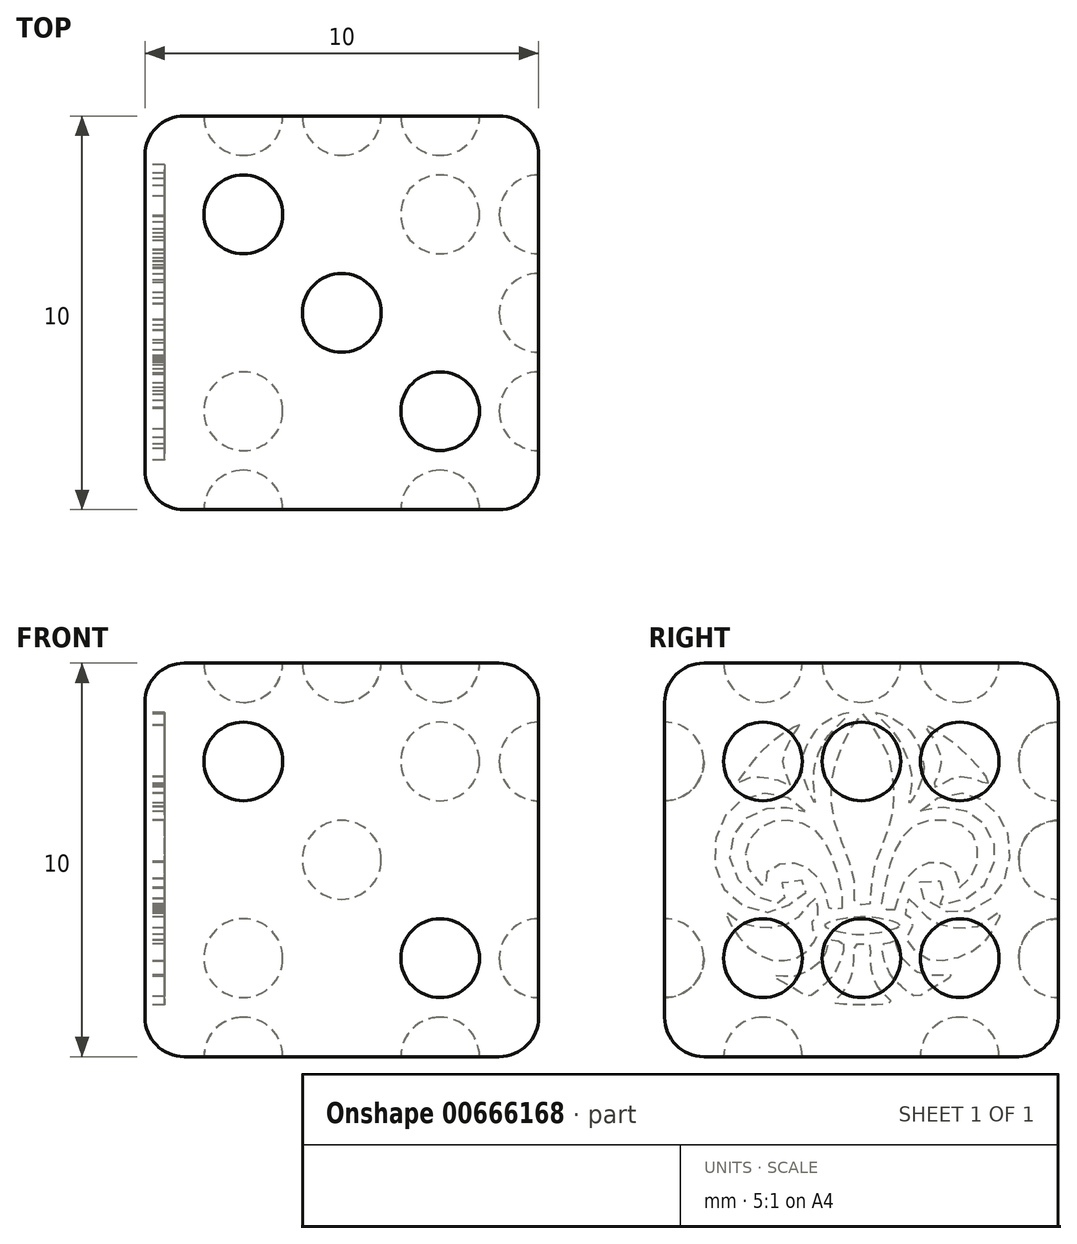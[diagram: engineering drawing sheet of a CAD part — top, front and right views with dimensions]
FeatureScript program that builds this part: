
annotation { "Feature Type Name" : "Feature", "Feature Type Description" : "" }
export const myFeature = defineFeature(function(context is Context, id is Id, definition is map)
    precondition{}
    {
        {
            var Q0;
            Q0=qCreatedBy(makeId("Front.planeOp"),FACE);
            var sketch = newSketch(context, id + "F0", { "sketchPlane" : qUnion([Q0])});
            skLineSegment(sketch, "E0.bottom", {"start": v(-26.81, 13.83) * mm, "end": v(-36.81, 13.83) * mm});
            skLineSegment(sketch, "E0.top", {"start": v(-26.81, 3.83) * mm, "end": v(-36.81, 3.83) * mm});
            skLineSegment(sketch, "E0.left", {"start": v(-26.81, 13.83) * mm, "end": v(-26.81, 3.83) * mm});
            skLineSegment(sketch, "E0.right", {"start": v(-36.81, 13.83) * mm, "end": v(-36.81, 3.83) * mm});
            skPoint(sketch, "E0.middle", {"position": v(-31.81, 8.83) * mm});
            skSolve(sketch);
        }
        {
            var Q0;
            Q0=makeQuery(id+"F0.imprint","IMPRINT",FACE,{"disambiguationData":[TD([[makeQuery(id+"F0.imprint","IMPRINT",EDGE,{"derivedFrom":sQuery(id+"F0.wireOp",EDGE,"E0.bottom")}),1.0]])]});
            extrude(context, id + "F1", {"entities" : qUnion([Q0]), "depth" : 10 * mm, "offsetDistance" : 25 * mm});
        }
        {
            var Q0;
            Q0=makeQuery(id+"F1.opExtrude","CAP_EDGE",EDGE,{"disambiguationData":[OSD([sQuery(id+"F0.wireOp",EDGE,"E0.bottom")])],"isStart":false});
            var Q1;
            Q1=makeQuery(id+"F1.opExtrude","CAP_EDGE",EDGE,{"disambiguationData":[OSD([sQuery(id+"F0.wireOp",EDGE,"E0.left")])],"isStart":false});
            var Q2;
            Q2=makeQuery(id+"F1.opExtrude","CAP_EDGE",EDGE,{"disambiguationData":[OSD([sQuery(id+"F0.wireOp",EDGE,"E0.right")])],"isStart":false});
            var Q3;
            Q3=makeQuery(id+"F1.opExtrude","CAP_EDGE",EDGE,{"disambiguationData":[OSD([sQuery(id+"F0.wireOp",EDGE,"E0.top")])],"isStart":false});
            var Q4;
            Q4=makeQuery(id+"F1.opExtrude","SWEPT_EDGE",EDGE,{"disambiguationData":[OSD([sQuery(id+"F0.wireOp",EDGE,"E0.bottom"),sQuery(id+"F0.wireOp",EDGE,"E0.left")])]});
            var Q5;
            Q5=makeQuery(id+"F1.opExtrude","SWEPT_EDGE",EDGE,{"disambiguationData":[OSD([sQuery(id+"F0.wireOp",EDGE,"E0.top"),sQuery(id+"F0.wireOp",EDGE,"E0.left")])]});
            var Q6;
            Q6=makeQuery(id+"F1.opExtrude","CAP_EDGE",EDGE,{"disambiguationData":[OSD([sQuery(id+"F0.wireOp",EDGE,"E0.left")])],"isStart":true});
            var Q7;
            Q7=makeQuery(id+"F1.opExtrude","SWEPT_EDGE",EDGE,{"disambiguationData":[OSD([sQuery(id+"F0.wireOp",EDGE,"E0.bottom"),sQuery(id+"F0.wireOp",EDGE,"E0.right")])]});
            var Q8;
            Q8=makeQuery(id+"F1.opExtrude","CAP_EDGE",EDGE,{"disambiguationData":[OSD([sQuery(id+"F0.wireOp",EDGE,"E0.right")])],"isStart":true});
            var Q9;
            Q9=makeQuery(id+"F1.opExtrude","SWEPT_EDGE",EDGE,{"disambiguationData":[OSD([sQuery(id+"F0.wireOp",EDGE,"E0.top"),sQuery(id+"F0.wireOp",EDGE,"E0.right")])]});
            var Q10;
            Q10=makeQuery(id+"F1.opExtrude","CAP_EDGE",EDGE,{"disambiguationData":[OSD([sQuery(id+"F0.wireOp",EDGE,"E0.top")])],"isStart":true});
            var Q11;
            Q11=makeQuery(id+"F1.opExtrude","CAP_EDGE",EDGE,{"disambiguationData":[OSD([sQuery(id+"F0.wireOp",EDGE,"E0.bottom")])],"isStart":true});
            fillet(context, id + "F2", {"entities" : qUnion([Q0, Q1, Q2, Q3, Q4, Q5, Q6, Q7, Q8, Q9, Q10, Q11]), "radius" : 1 * mm, "tangentPropagation" : true, "allowEdgeOverflow" : false});
        }
        {
            var Q0;
            Q0=makeQuery(id+"F1.opExtrude","CAP_FACE",FACE,{"disambiguationData":[OSD([sQuery(id+"F0.wireOp",EDGE,"E0.bottom"),sQuery(id+"F0.wireOp",EDGE,"E0.top"),sQuery(id+"F0.wireOp",EDGE,"E0.left"),sQuery(id+"F0.wireOp",EDGE,"E0.right")])],"isStart":false});
            var sketch = newSketch(context, id + "F3", { "sketchPlane" : qUnion([Q0])});
            skCircle(sketch, "E1", {"center": v(-34.31, 11.33) * mm, "radius": 1 * mm});
            skCircle(sketch, "E2", {"center": v(-29.31, 6.33) * mm, "radius": 1 * mm});
            skSolve(sketch);
        }
        {
            var Q0;
            Q0=makeQuery(id+"F3.imprint","IMPRINT",FACE,{"disambiguationData":[TD([[makeQuery(id+"F3.imprint","IMPRINT",EDGE,{"derivedFrom":sQuery(id+"F3.wireOp",EDGE,"E1")}),1.0]])]});
            var Q1;
            Q1=makeQuery(id+"F3.imprint","IMPRINT",FACE,{"disambiguationData":[TD([[makeQuery(id+"F3.imprint","IMPRINT",EDGE,{"derivedFrom":sQuery(id+"F3.wireOp",EDGE,"E2")}),1.0]])]});
            extrude(context, id + "F4", {"entities" : qUnion([Q0, Q1]), "operationType" : NewBodyOperationType.REMOVE, "oppositeDirection" : true, "depth" : 1 * mm, "offsetDistance" : 25 * mm});
        }
        {
            var Q0;
            Q0=makeQuery(id+"F4.boolean.opBoolean","COPY",EDGE,{"derivedFrom":makeQuery(id+"F4.opExtrude","CAP_EDGE",EDGE,{"disambiguationData":[OSD([sQuery(id+"F3.wireOp",EDGE,"E1")])],"isStart":false})});
            var Q1;
            Q1=makeQuery(id+"F4.boolean.opBoolean","COPY",EDGE,{"derivedFrom":makeQuery(id+"F4.opExtrude","CAP_EDGE",EDGE,{"disambiguationData":[OSD([sQuery(id+"F3.wireOp",EDGE,"E2")])],"isStart":false})});
            fillet(context, id + "F5", {"entities" : qUnion([Q0, Q1]), "radius" : 1 * mm, "tangentPropagation" : true, "allowEdgeOverflow" : false});
        }
        {
            var Q0;
            Q0=makeQuery(id+"F1.opExtrude","CAP_FACE",FACE,{"disambiguationData":[OSD([sQuery(id+"F0.wireOp",EDGE,"E0.bottom"),sQuery(id+"F0.wireOp",EDGE,"E0.top"),sQuery(id+"F0.wireOp",EDGE,"E0.left"),sQuery(id+"F0.wireOp",EDGE,"E0.right")])],"isStart":true});
            var sketch = newSketch(context, id + "F6", { "sketchPlane" : qUnion([Q0])});
            skCircle(sketch, "E3", {"center": v(29.31, 11.33) * mm, "radius": 1 * mm});
            skCircle(sketch, "E4", {"center": v(34.31, 11.33) * mm, "radius": 1 * mm});
            skCircle(sketch, "E5", {"center": v(34.31, 6.33) * mm, "radius": 1 * mm});
            skCircle(sketch, "E6", {"center": v(29.31, 6.33) * mm, "radius": 1 * mm});
            skCircle(sketch, "E7", {"center": v(31.81, 8.83) * mm, "radius": 1 * mm});
            skSolve(sketch);
        }
        {
            var Q0;
            Q0=makeQuery(id+"F6.imprint","IMPRINT",FACE,{"disambiguationData":[TD([[makeQuery(id+"F6.imprint","IMPRINT",EDGE,{"derivedFrom":sQuery(id+"F6.wireOp",EDGE,"E3")}),1.0]])]});
            var Q1;
            Q1=makeQuery(id+"F6.imprint","IMPRINT",FACE,{"disambiguationData":[TD([[makeQuery(id+"F6.imprint","IMPRINT",EDGE,{"derivedFrom":sQuery(id+"F6.wireOp",EDGE,"E4")}),1.0]])]});
            var Q2;
            Q2=makeQuery(id+"F6.imprint","IMPRINT",FACE,{"disambiguationData":[TD([[makeQuery(id+"F6.imprint","IMPRINT",EDGE,{"derivedFrom":sQuery(id+"F6.wireOp",EDGE,"E7")}),1.0]])]});
            var Q3;
            Q3=makeQuery(id+"F6.imprint","IMPRINT",FACE,{"disambiguationData":[TD([[makeQuery(id+"F6.imprint","IMPRINT",EDGE,{"derivedFrom":sQuery(id+"F6.wireOp",EDGE,"E5")}),1.0]])]});
            var Q4;
            Q4=makeQuery(id+"F6.imprint","IMPRINT",FACE,{"disambiguationData":[TD([[makeQuery(id+"F6.imprint","IMPRINT",EDGE,{"derivedFrom":sQuery(id+"F6.wireOp",EDGE,"E6")}),1.0]])]});
            extrude(context, id + "F7", {"entities" : qUnion([Q0, Q1, Q2, Q3, Q4]), "operationType" : NewBodyOperationType.REMOVE, "oppositeDirection" : true, "depth" : 1 * mm, "offsetDistance" : 25 * mm});
        }
        {
            var Q0;
            Q0=makeQuery(id+"F7.boolean.opBoolean","COPY",EDGE,{"derivedFrom":makeQuery(id+"F7.opExtrude","CAP_EDGE",EDGE,{"disambiguationData":[OSD([sQuery(id+"F6.wireOp",EDGE,"E6")])],"isStart":false})});
            var Q1;
            Q1=makeQuery(id+"F7.boolean.opBoolean","COPY",EDGE,{"derivedFrom":makeQuery(id+"F7.opExtrude","CAP_EDGE",EDGE,{"disambiguationData":[OSD([sQuery(id+"F6.wireOp",EDGE,"E3")])],"isStart":false})});
            var Q2;
            Q2=makeQuery(id+"F7.boolean.opBoolean","COPY",EDGE,{"derivedFrom":makeQuery(id+"F7.opExtrude","CAP_EDGE",EDGE,{"disambiguationData":[OSD([sQuery(id+"F6.wireOp",EDGE,"E7")])],"isStart":false})});
            var Q3;
            Q3=makeQuery(id+"F7.boolean.opBoolean","COPY",EDGE,{"derivedFrom":makeQuery(id+"F7.opExtrude","CAP_EDGE",EDGE,{"disambiguationData":[OSD([sQuery(id+"F6.wireOp",EDGE,"E4")])],"isStart":false})});
            var Q4;
            Q4=makeQuery(id+"F7.boolean.opBoolean","COPY",EDGE,{"derivedFrom":makeQuery(id+"F7.opExtrude","CAP_EDGE",EDGE,{"disambiguationData":[OSD([sQuery(id+"F6.wireOp",EDGE,"E5")])],"isStart":false})});
            fillet(context, id + "F8", {"entities" : qUnion([Q0, Q1, Q2, Q3, Q4]), "radius" : 1 * mm, "tangentPropagation" : true, "allowEdgeOverflow" : false});
        }
        {
            var Q0;
            Q0=makeQuery(id+"F1.opExtrude","SWEPT_FACE",FACE,{"disambiguationData":[OSD([sQuery(id+"F0.wireOp",EDGE,"E0.bottom")])]});
            var sketch = newSketch(context, id + "F9", { "sketchPlane" : qUnion([Q0])});
            skCircle(sketch, "E8", {"center": v(-34.31, -2.5) * mm, "radius": 1 * mm});
            skCircle(sketch, "E9", {"center": v(-31.81, -5) * mm, "radius": 1 * mm});
            skCircle(sketch, "E10", {"center": v(-29.31, -7.5) * mm, "radius": 1 * mm});
            skSolve(sketch);
        }
        {
            var Q0;
            Q0=makeQuery(id+"F9.imprint","IMPRINT",FACE,{"disambiguationData":[TD([[makeQuery(id+"F9.imprint","IMPRINT",EDGE,{"derivedFrom":sQuery(id+"F9.wireOp",EDGE,"E8")}),1.0]])]});
            var Q1;
            Q1=makeQuery(id+"F9.imprint","IMPRINT",FACE,{"disambiguationData":[TD([[makeQuery(id+"F9.imprint","IMPRINT",EDGE,{"derivedFrom":sQuery(id+"F9.wireOp",EDGE,"E9")}),1.0]])]});
            var Q2;
            Q2=makeQuery(id+"F9.imprint","IMPRINT",FACE,{"disambiguationData":[TD([[makeQuery(id+"F9.imprint","IMPRINT",EDGE,{"derivedFrom":sQuery(id+"F9.wireOp",EDGE,"E10")}),1.0]])]});
            extrude(context, id + "F10", {"entities" : qUnion([Q0, Q1, Q2]), "operationType" : NewBodyOperationType.REMOVE, "oppositeDirection" : true, "depth" : 1 * mm, "offsetDistance" : 25 * mm});
        }
        {
            var Q0;
            Q0=makeQuery(id+"F10.boolean.opBoolean","COPY",EDGE,{"derivedFrom":makeQuery(id+"F10.opExtrude","CAP_EDGE",EDGE,{"disambiguationData":[OSD([sQuery(id+"F9.wireOp",EDGE,"E8")])],"isStart":false})});
            var Q1;
            Q1=makeQuery(id+"F10.boolean.opBoolean","COPY",EDGE,{"derivedFrom":makeQuery(id+"F10.opExtrude","CAP_EDGE",EDGE,{"disambiguationData":[OSD([sQuery(id+"F9.wireOp",EDGE,"E9")])],"isStart":false})});
            var Q2;
            Q2=makeQuery(id+"F10.boolean.opBoolean","COPY",EDGE,{"derivedFrom":makeQuery(id+"F10.opExtrude","CAP_EDGE",EDGE,{"disambiguationData":[OSD([sQuery(id+"F9.wireOp",EDGE,"E10")])],"isStart":false})});
            fillet(context, id + "F11", {"entities" : qUnion([Q0, Q1, Q2]), "radius" : 1 * mm, "tangentPropagation" : true, "allowEdgeOverflow" : false});
        }
        {
            var Q0;
            Q0=makeQuery(id+"F1.opExtrude","SWEPT_FACE",FACE,{"disambiguationData":[OSD([sQuery(id+"F0.wireOp",EDGE,"E0.top")])]});
            var sketch = newSketch(context, id + "F12", { "sketchPlane" : qUnion([Q0])});
            skCircle(sketch, "E11", {"center": v(-34.31, 7.5) * mm, "radius": 1 * mm});
            skCircle(sketch, "E12", {"center": v(-29.31, 7.5) * mm, "radius": 1 * mm});
            skCircle(sketch, "E13", {"center": v(-34.31, 2.5) * mm, "radius": 1 * mm});
            skCircle(sketch, "E14", {"center": v(-29.31, 2.5) * mm, "radius": 1 * mm});
            skSolve(sketch);
        }
        {
            var Q0;
            Q0=makeQuery(id+"F12.imprint","IMPRINT",FACE,{"disambiguationData":[TD([[makeQuery(id+"F12.imprint","IMPRINT",EDGE,{"derivedFrom":sQuery(id+"F12.wireOp",EDGE,"E11")}),1.0]])]});
            var Q1;
            Q1=makeQuery(id+"F12.imprint","IMPRINT",FACE,{"disambiguationData":[TD([[makeQuery(id+"F12.imprint","IMPRINT",EDGE,{"derivedFrom":sQuery(id+"F12.wireOp",EDGE,"E12")}),1.0]])]});
            var Q2;
            Q2=makeQuery(id+"F12.imprint","IMPRINT",FACE,{"disambiguationData":[TD([[makeQuery(id+"F12.imprint","IMPRINT",EDGE,{"derivedFrom":sQuery(id+"F12.wireOp",EDGE,"E13")}),1.0]])]});
            var Q3;
            Q3=makeQuery(id+"F12.imprint","IMPRINT",FACE,{"disambiguationData":[TD([[makeQuery(id+"F12.imprint","IMPRINT",EDGE,{"derivedFrom":sQuery(id+"F12.wireOp",EDGE,"E14")}),1.0]])]});
            extrude(context, id + "F13", {"entities" : qUnion([Q0, Q1, Q2, Q3]), "operationType" : NewBodyOperationType.REMOVE, "oppositeDirection" : true, "depth" : 1 * mm, "offsetDistance" : 25 * mm});
        }
        {
            var Q0;
            Q0=makeQuery(id+"F13.boolean.opBoolean","COPY",EDGE,{"derivedFrom":makeQuery(id+"F13.opExtrude","CAP_EDGE",EDGE,{"disambiguationData":[OSD([sQuery(id+"F12.wireOp",EDGE,"E11")])],"isStart":false})});
            var Q1;
            Q1=makeQuery(id+"F13.boolean.opBoolean","COPY",FACE,{"derivedFrom":makeQuery(id+"F13.opExtrude","CAP_FACE",FACE,{"disambiguationData":[OSD([sQuery(id+"F12.wireOp",EDGE,"E12")])],"isStart":false})});
            var Q2;
            Q2=makeQuery(id+"F13.boolean.opBoolean","COPY",FACE,{"derivedFrom":makeQuery(id+"F13.opExtrude","CAP_FACE",FACE,{"disambiguationData":[OSD([sQuery(id+"F12.wireOp",EDGE,"E13")])],"isStart":false})});
            var Q3;
            Q3=makeQuery(id+"F13.boolean.opBoolean","COPY",FACE,{"derivedFrom":makeQuery(id+"F13.opExtrude","CAP_FACE",FACE,{"disambiguationData":[OSD([sQuery(id+"F12.wireOp",EDGE,"E14")])],"isStart":false})});
            fillet(context, id + "F14", {"entities" : qUnion([Q0, Q1, Q2, Q3]), "radius" : 1 * mm, "tangentPropagation" : true, "allowEdgeOverflow" : false});
        }
        {
            var Q0;
            Q0=makeQuery(id+"F1.opExtrude","SWEPT_FACE",FACE,{"disambiguationData":[OSD([sQuery(id+"F0.wireOp",EDGE,"E0.left")])]});
            var sketch = newSketch(context, id + "F15", { "sketchPlane" : qUnion([Q0])});
            skPoint(sketch, "E15.center.orphan", {"position": v(-2.5, 6.33) * mm});
            skPoint(sketch, "E16.center.orphan", {"position": v(-5, 6.33) * mm});
            skPoint(sketch, "E17.center.orphan", {"position": v(-7.5, 6.33) * mm});
            skPoint(sketch, "E18.center.orphan", {"position": v(-7.5, 11.33) * mm});
            skPoint(sketch, "E19.center.orphan", {"position": v(-5, 11.33) * mm});
            skPoint(sketch, "E20.center.orphan", {"position": v(-2.5, 11.33) * mm});
            skCircle(sketch, "E21", {"center": v(-2.5, 6.33) * mm, "radius": 1 * mm});
            skCircle(sketch, "E22", {"center": v(-5, 6.33) * mm, "radius": 1 * mm});
            skCircle(sketch, "E23", {"center": v(-7.5, 6.33) * mm, "radius": 1 * mm});
            skCircle(sketch, "E24", {"center": v(-2.5, 11.33) * mm, "radius": 1 * mm});
            skCircle(sketch, "E25", {"center": v(-5, 11.33) * mm, "radius": 1 * mm});
            skCircle(sketch, "E26", {"center": v(-7.5, 11.33) * mm, "radius": 1 * mm});
            skSolve(sketch);
        }
        {
            var Q0;
            Q0=makeQuery(id+"F15.imprint","IMPRINT",FACE,{"disambiguationData":[TD([[makeQuery(id+"F15.imprint","IMPRINT",EDGE,{"derivedFrom":sQuery(id+"F15.wireOp",EDGE,"E18")}),1.0]])]});
            var Q1;
            Q1=makeQuery(id+"F15.imprint","IMPRINT",FACE,{"disambiguationData":[TD([[makeQuery(id+"F15.imprint","IMPRINT",EDGE,{"derivedFrom":sQuery(id+"F15.wireOp",EDGE,"E17")}),1.0]])]});
            var Q2;
            Q2=makeQuery(id+"F15.imprint","IMPRINT",FACE,{"disambiguationData":[TD([[makeQuery(id+"F15.imprint","IMPRINT",EDGE,{"derivedFrom":sQuery(id+"F15.wireOp",EDGE,"E21")}),1.0]])]});
            var Q3;
            Q3=makeQuery(id+"F15.imprint","IMPRINT",FACE,{"disambiguationData":[TD([[makeQuery(id+"F15.imprint","IMPRINT",EDGE,{"derivedFrom":sQuery(id+"F15.wireOp",EDGE,"E22")}),1.0]])]});
            var Q4;
            Q4=makeQuery(id+"F15.imprint","IMPRINT",FACE,{"disambiguationData":[TD([[makeQuery(id+"F15.imprint","IMPRINT",EDGE,{"derivedFrom":sQuery(id+"F15.wireOp",EDGE,"E23")}),1.0]])]});
            var Q5;
            Q5=makeQuery(id+"F15.imprint","IMPRINT",FACE,{"disambiguationData":[TD([[makeQuery(id+"F15.imprint","IMPRINT",EDGE,{"derivedFrom":sQuery(id+"F15.wireOp",EDGE,"E26")}),1.0]])]});
            var Q6;
            Q6=makeQuery(id+"F15.imprint","IMPRINT",FACE,{"disambiguationData":[TD([[makeQuery(id+"F15.imprint","IMPRINT",EDGE,{"derivedFrom":sQuery(id+"F15.wireOp",EDGE,"E25")}),1.0]])]});
            var Q7;
            Q7=makeQuery(id+"F15.imprint","IMPRINT",FACE,{"disambiguationData":[TD([[makeQuery(id+"F15.imprint","IMPRINT",EDGE,{"derivedFrom":sQuery(id+"F15.wireOp",EDGE,"E24")}),1.0]])]});
            extrude(context, id + "F16", {"entities" : qUnion([Q0, Q1, Q2, Q3, Q4, Q5, Q6, Q7]), "operationType" : NewBodyOperationType.REMOVE, "oppositeDirection" : true, "depth" : 1 * mm, "offsetDistance" : 25 * mm});
        }
        {
            var Q0;
            Q0=makeQuery(id+"F16.boolean.opBoolean","COPY",EDGE,{"derivedFrom":makeQuery(id+"F16.opExtrude","CAP_EDGE",EDGE,{"disambiguationData":[OSD([sQuery(id+"F15.wireOp",EDGE,"E21")])],"isStart":false})});
            var Q1;
            Q1=makeQuery(id+"F16.boolean.opBoolean","COPY",EDGE,{"derivedFrom":makeQuery(id+"F16.opExtrude","CAP_EDGE",EDGE,{"disambiguationData":[OSD([sQuery(id+"F15.wireOp",EDGE,"E22")])],"isStart":false})});
            var Q2;
            Q2=makeQuery(id+"F16.boolean.opBoolean","COPY",EDGE,{"derivedFrom":makeQuery(id+"F16.opExtrude","CAP_EDGE",EDGE,{"disambiguationData":[OSD([sQuery(id+"F15.wireOp",EDGE,"E23")])],"isStart":false})});
            var Q3;
            Q3=makeQuery(id+"F16.boolean.opBoolean","COPY",EDGE,{"derivedFrom":makeQuery(id+"F16.opExtrude","CAP_EDGE",EDGE,{"disambiguationData":[OSD([sQuery(id+"F15.wireOp",EDGE,"E24")])],"isStart":false})});
            var Q4;
            Q4=makeQuery(id+"F16.boolean.opBoolean","COPY",EDGE,{"derivedFrom":makeQuery(id+"F16.opExtrude","CAP_EDGE",EDGE,{"disambiguationData":[OSD([sQuery(id+"F15.wireOp",EDGE,"E25")])],"isStart":false})});
            var Q5;
            Q5=makeQuery(id+"F16.boolean.opBoolean","COPY",EDGE,{"derivedFrom":makeQuery(id+"F16.opExtrude","CAP_EDGE",EDGE,{"disambiguationData":[OSD([sQuery(id+"F15.wireOp",EDGE,"E26")])],"isStart":false})});
            fillet(context, id + "F17", {"entities" : qUnion([Q0, Q1, Q2, Q3, Q4, Q5]), "radius" : 1 * mm, "tangentPropagation" : true, "allowEdgeOverflow" : false});
        }
        {
            var Q0;
            Q0=makeQuery(id+"F1.opExtrude","SWEPT_FACE",FACE,{"disambiguationData":[OSD([sQuery(id+"F0.wireOp",EDGE,"E0.right")])]});
            var sketch = newSketch(context, id + "F18", { "sketchPlane" : qUnion([Q0])});
            skFitSpline(sketch, "E27", {"points": [v(1.77, 10.79) * mm, v(2.2, 11.39) * mm, v(2.6, 11.75) * mm, v(3.08, 12.09) * mm, v(3.4, 12.24) * mm, v(3.23, 12) * mm, v(3.04, 11.6) * mm, v(3, 11.16) * mm, v(3.16, 10.69) * mm, v(2.77, 10.86) * mm, v(2.26, 10.93) * mm, v(1.77, 10.79) * mm]});
            skFitSpline(sketch, "E28", {"points": [v(3.5, 10.07) * mm, v(3.06, 10.4) * mm, v(2.38, 10.52) * mm, v(2, 10.38) * mm, v(1.54, 10) * mm, v(1.28, 9.48) * mm, v(1.25, 8.74) * mm, v(1.44, 8.16) * mm, v(1.87, 7.71) * mm, v(2.52, 7.47) * mm, v(3.08, 7.63) * mm, v(3.61, 8.13) * mm, v(3.22, 8.36) * mm, v(2.9, 8.2) * mm, v(2.92, 7.93) * mm, v(3.07, 7.72) * mm, v(2.52, 7.78) * mm, v(1.93, 8.13) * mm, v(1.63, 8.73) * mm, v(1.6, 9.11) * mm, v(1.84, 9.7) * mm, v(2.27, 10.03) * mm, v(2.83, 10.18) * mm, v(3.5, 10.07) * mm]});
            skFitSpline(sketch, "E29", {"points": [v(4.15, 7.57) * mm, v(3.98, 8.12) * mm, v(3.62, 8.6) * mm, v(3.15, 8.78) * mm, v(2.7, 8.66) * mm, v(2.54, 8.4) * mm, v(2.54, 8.11) * mm, v(2.16, 8.48) * mm, v(2.04, 9) * mm, v(2.17, 9.48) * mm, v(2.65, 9.79) * mm, v(3.39, 9.8) * mm, v(3.86, 9.53) * mm, v(4.16, 9.03) * mm, v(4.35, 8.4) * mm, v(4.46, 7.6) * mm, v(4.3, 7.58) * mm, v(4.15, 7.57) * mm]});
            skFitSpline(sketch, "E30", {"points": [v(3.78, 7.84) * mm, v(3.45, 7.5) * mm, v(2.92, 7.16) * mm, v(2.28, 7.1) * mm, v(1.88, 7.23) * mm, v(1.46, 7.53) * mm, v(1.66, 7.07) * mm, v(2.08, 6.56) * mm, v(2.78, 6.29) * mm, v(3.43, 6.35) * mm, v(3.85, 6.88) * mm, v(3.74, 7.02) * mm, v(3.69, 7.18) * mm, v(3.77, 7.37) * mm, v(3.86, 7.42) * mm, v(3.85, 7.64) * mm, v(3.78, 7.84) * mm]});
            skFitSpline(sketch, "E31", {"points": [v(4.02, 7.16) * mm, v(4.23, 7.28) * mm, v(4.8, 7.37) * mm, v(5.33, 7.35) * mm, v(5.95, 7.17) * mm, v(5.4, 6.97) * mm, v(4.73, 6.96) * mm, v(4.02, 7.16) * mm]});
            skFitSpline(sketch, "E32", {"points": [v(4.63, 12.57) * mm, v(4.07, 12.35) * mm, v(3.68, 12) * mm, v(3.44, 11.42) * mm, v(3.49, 10.8) * mm, v(3.78, 10.27) * mm, v(3.71, 10.72) * mm, v(3.8, 11.31) * mm, v(3.99, 11.78) * mm, v(4.24, 12.15) * mm, v(4.63, 12.57) * mm]});
            skFitSpline(sketch, "E33", {"points": [v(4.97, 12.54) * mm, v(4.73, 12.21) * mm, v(4.39, 11.67) * mm, v(4.24, 11.15) * mm, v(4.17, 10.3) * mm, v(4.28, 9.73) * mm, v(4.55, 9) * mm, v(4.73, 8.43) * mm, v(4.8, 7.68) * mm, v(4.95, 7.69) * mm, v(5.13, 7.69) * mm, v(5.17, 8.21) * mm, v(5.36, 8.95) * mm, v(5.68, 9.83) * mm, v(5.77, 10.6) * mm, v(5.64, 11.3) * mm, v(5.36, 11.99) * mm, v(4.97, 12.54) * mm]});
            skFitSpline(sketch, "E34", {"points": [v(5.31, 12.57) * mm, v(5.95, 12.3) * mm, v(6.3, 11.9) * mm, v(6.53, 11.3) * mm, v(6.43, 10.8) * mm, v(6.18, 10.27) * mm, v(6.21, 10.79) * mm, v(6.12, 11.44) * mm, v(5.78, 12.06) * mm, v(5.31, 12.57) * mm]});
            skFitSpline(sketch, "E35", {"points": [v(6.57, 12.25) * mm, v(7.26, 11.84) * mm, v(7.87, 11.2) * mm, v(8.17, 10.77) * mm, v(7.97, 10.87) * mm, v(7.46, 10.93) * mm, v(6.96, 10.79) * mm, v(6.8, 10.7) * mm, v(6.96, 11.14) * mm, v(6.93, 11.61) * mm, v(6.7, 12.05) * mm, v(6.57, 12.25) * mm]});
            skFitSpline(sketch, "E36", {"points": [v(6.43, 10.06) * mm, v(6.83, 10.4) * mm, v(7.45, 10.52) * mm, v(8.05, 10.35) * mm, v(8.5, 9.9) * mm, v(8.72, 9.27) * mm, v(8.67, 8.45) * mm, v(8.26, 7.83) * mm, v(7.57, 7.5) * mm, v(6.98, 7.6) * mm, v(6.54, 7.91) * mm, v(6.33, 8.14) * mm, v(6.62, 8.34) * mm, v(7.04, 8.22) * mm, v(7.03, 7.97) * mm, v(6.9, 7.73) * mm, v(7.3, 7.76) * mm, v(7.75, 7.95) * mm, v(8.25, 8.52) * mm, v(8.32, 9.08) * mm, v(8.15, 9.64) * mm, v(7.77, 10) * mm, v(7.2, 10.18) * mm, v(6.78, 10.14) * mm, v(6.43, 10.06) * mm]});
            skFitSpline(sketch, "E37", {"points": [v(5.48, 7.6) * mm, v(5.55, 8.3) * mm, v(5.8, 9.05) * mm, v(6.16, 9.58) * mm, v(6.6, 9.78) * mm, v(7.12, 9.82) * mm, v(7.6, 9.62) * mm, v(7.9, 9.16) * mm, v(7.86, 8.58) * mm, v(7.42, 8.13) * mm, v(7.43, 8.41) * mm, v(7.12, 8.7) * mm, v(6.6, 8.73) * mm, v(6.2, 8.47) * mm, v(5.9, 7.98) * mm, v(5.8, 7.54) * mm, v(5.64, 7.6) * mm, v(5.48, 7.6) * mm]});
            skFitSpline(sketch, "E38", {"points": [v(6.17, 7.85) * mm, v(6.47, 7.52) * mm, v(7.02, 7.14) * mm, v(7.7, 7.13) * mm, v(8.2, 7.3) * mm, v(8.45, 7.5) * mm, v(8.28, 7.12) * mm, v(7.85, 6.58) * mm, v(7.3, 6.3) * mm, v(6.88, 6.28) * mm, v(6.48, 6.43) * mm, v(6.2, 6.73) * mm, v(6.13, 6.89) * mm, v(6.23, 7.06) * mm, v(6.24, 7.26) * mm, v(6.1, 7.4) * mm, v(6.1, 7.6) * mm, v(6.17, 7.85) * mm]});
            skFitSpline(sketch, "E39", {"points": [v(4.14, 6.78) * mm, v(4.08, 6.52) * mm, v(3.82, 6.19) * mm, v(3.4, 5.93) * mm, v(2.7, 5.9) * mm, v(3.12, 5.62) * mm, v(3.62, 5.36) * mm, v(3.88, 5.53) * mm, v(4.21, 5.85) * mm, v(4.4, 6.23) * mm, v(4.46, 6.68) * mm, v(4.3, 6.72) * mm, v(4.14, 6.78) * mm]});
            skFitSpline(sketch, "E40", {"points": [v(4.8, 6.67) * mm, v(4.78, 6.33) * mm, v(4.73, 5.95) * mm, v(4.5, 5.5) * mm, v(4.24, 5.21) * mm, v(4.73, 5.15) * mm, v(5.36, 5.15) * mm, v(5.7, 5.21) * mm, v(5.49, 5.44) * mm, v(5.29, 5.8) * mm, v(5.18, 6.18) * mm, v(5.15, 6.67) * mm, v(4.97, 6.7) * mm, v(4.8, 6.67) * mm]});
            skFitSpline(sketch, "E41", {"points": [v(5.45, 6.7) * mm, v(5.52, 6.32) * mm, v(5.74, 5.88) * mm, v(6.12, 5.5) * mm, v(6.34, 5.36) * mm, v(6.66, 5.53) * mm, v(7.24, 5.88) * mm, v(6.84, 5.87) * mm, v(6.4, 6) * mm, v(6.08, 6.23) * mm, v(5.89, 6.5) * mm, v(5.79, 6.78) * mm, v(5.64, 6.78) * mm, v(5.45, 6.7) * mm]});
            skSolve(sketch);
        }
        {
            var Q0;
            Q0=makeQuery(id+"F18.imprint","IMPRINT",FACE,{"disambiguationData":[TD([[makeQuery(id+"F18.imprint","IMPRINT",EDGE,{"derivedFrom":sQuery(id+"F18.wireOp",EDGE,"E29")}),-1.0]])]});
            var Q1;
            Q1=makeQuery(id+"F18.imprint","IMPRINT",FACE,{"disambiguationData":[TD([[makeQuery(id+"F18.imprint","IMPRINT",EDGE,{"derivedFrom":sQuery(id+"F18.wireOp",EDGE,"E33")}),1.0]])]});
            var Q2;
            Q2=makeQuery(id+"F18.imprint","IMPRINT",FACE,{"disambiguationData":[TD([[makeQuery(id+"F18.imprint","IMPRINT",EDGE,{"derivedFrom":sQuery(id+"F18.wireOp",EDGE,"E32")}),1.0]])]});
            var Q3;
            Q3=makeQuery(id+"F18.imprint","IMPRINT",FACE,{"disambiguationData":[TD([[makeQuery(id+"F18.imprint","IMPRINT",EDGE,{"derivedFrom":sQuery(id+"F18.wireOp",EDGE,"E27")}),-1.0]])]});
            var Q4;
            Q4=makeQuery(id+"F18.imprint","IMPRINT",FACE,{"disambiguationData":[TD([[makeQuery(id+"F18.imprint","IMPRINT",EDGE,{"derivedFrom":sQuery(id+"F18.wireOp",EDGE,"E28")}),1.0]])]});
            var Q5;
            Q5=makeQuery(id+"F18.imprint","IMPRINT",FACE,{"disambiguationData":[TD([[makeQuery(id+"F18.imprint","IMPRINT",EDGE,{"derivedFrom":sQuery(id+"F18.wireOp",EDGE,"E30")}),1.0]])]});
            var Q6;
            Q6=makeQuery(id+"F18.imprint","IMPRINT",FACE,{"disambiguationData":[TD([[makeQuery(id+"F18.imprint","IMPRINT",EDGE,{"derivedFrom":sQuery(id+"F18.wireOp",EDGE,"E31")}),-1.0]])]});
            var Q7;
            Q7=makeQuery(id+"F18.imprint","IMPRINT",FACE,{"disambiguationData":[TD([[makeQuery(id+"F18.imprint","IMPRINT",EDGE,{"derivedFrom":sQuery(id+"F18.wireOp",EDGE,"E39")}),1.0]])]});
            var Q8;
            Q8=makeQuery(id+"F18.imprint","IMPRINT",FACE,{"disambiguationData":[TD([[makeQuery(id+"F18.imprint","IMPRINT",EDGE,{"derivedFrom":sQuery(id+"F18.wireOp",EDGE,"E40")}),1.0]])]});
            var Q9;
            Q9=makeQuery(id+"F18.imprint","IMPRINT",FACE,{"disambiguationData":[TD([[makeQuery(id+"F18.imprint","IMPRINT",EDGE,{"derivedFrom":sQuery(id+"F18.wireOp",EDGE,"E41")}),1.0]])]});
            var Q10;
            Q10=makeQuery(id+"F18.imprint","IMPRINT",FACE,{"disambiguationData":[TD([[makeQuery(id+"F18.imprint","IMPRINT",EDGE,{"derivedFrom":sQuery(id+"F18.wireOp",EDGE,"E38")}),-1.0]])]});
            var Q11;
            Q11=makeQuery(id+"F18.imprint","IMPRINT",FACE,{"disambiguationData":[TD([[makeQuery(id+"F18.imprint","IMPRINT",EDGE,{"derivedFrom":sQuery(id+"F18.wireOp",EDGE,"E36")}),-1.0]])]});
            var Q12;
            Q12=makeQuery(id+"F18.imprint","IMPRINT",FACE,{"disambiguationData":[TD([[makeQuery(id+"F18.imprint","IMPRINT",EDGE,{"derivedFrom":sQuery(id+"F18.wireOp",EDGE,"E37")}),-1.0]])]});
            var Q13;
            Q13=makeQuery(id+"F18.imprint","IMPRINT",FACE,{"disambiguationData":[TD([[makeQuery(id+"F18.imprint","IMPRINT",EDGE,{"derivedFrom":sQuery(id+"F18.wireOp",EDGE,"E35")}),-1.0]])]});
            var Q14;
            Q14=makeQuery(id+"F18.imprint","IMPRINT",FACE,{"disambiguationData":[TD([[makeQuery(id+"F18.imprint","IMPRINT",EDGE,{"derivedFrom":sQuery(id+"F18.wireOp",EDGE,"E34")}),-1.0]])]});
            extrude(context, id + "F19", {"entities" : qUnion([Q0, Q1, Q2, Q3, Q4, Q5, Q6, Q7, Q8, Q9, Q10, Q11, Q12, Q13, Q14]), "operationType" : NewBodyOperationType.REMOVE, "oppositeDirection" : true, "depth" : 0.5 * mm, "offsetDistance" : 25 * mm});
        }
    });
